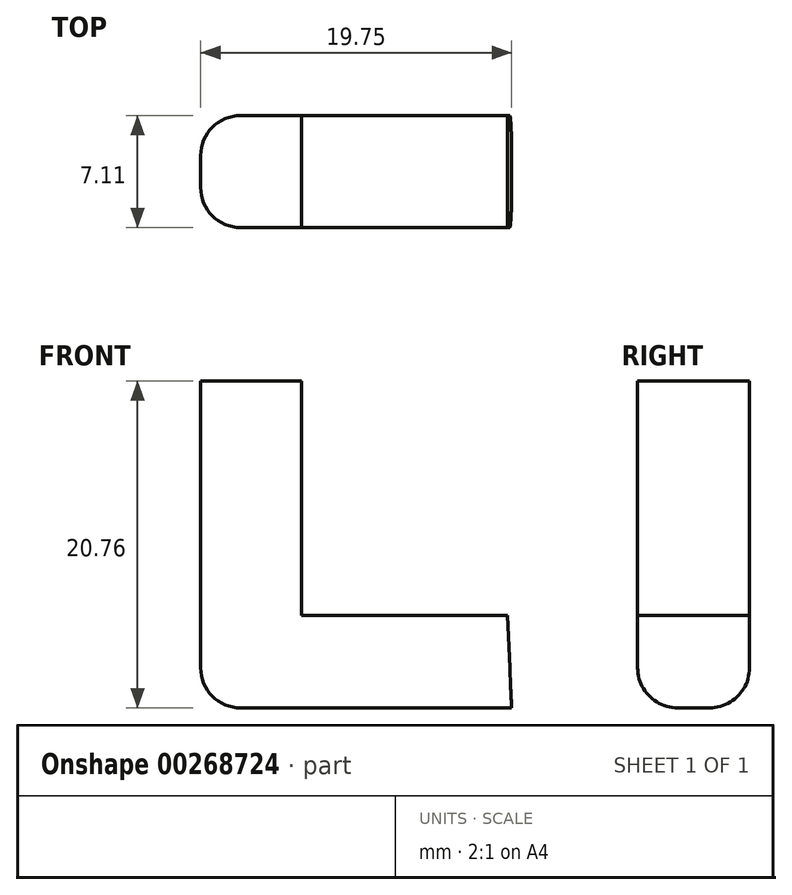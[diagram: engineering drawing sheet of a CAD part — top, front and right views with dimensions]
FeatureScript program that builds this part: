
annotation { "Feature Type Name" : "Feature", "Feature Type Description" : "" }
export const myFeature = defineFeature(function(context is Context, id is Id, definition is map)
    precondition{}
    {
        {
            var Q0;
            Q0=qCreatedBy(makeId("Front.planeOp"),FACE);
            var sketch = newSketch(context, id + "F0", { "sketchPlane" : qUnion([Q0])});
            skLineSegment(sketch, "E0", {"start": v(-9.11, -17.97) * mm, "end": v(-28.86, -17.97) * mm});
            skLineSegment(sketch, "E1", {"start": v(-28.86, -17.97) * mm, "end": v(-28.86, 2.8) * mm});
            skLineSegment(sketch, "E2", {"start": v(-28.86, 2.8) * mm, "end": v(-22.45, 2.8) * mm});
            skLineSegment(sketch, "E3", {"start": v(-22.45, 2.8) * mm, "end": v(-22.45, -12.1) * mm});
            skLineSegment(sketch, "E4", {"start": v(-22.45, -12.1) * mm, "end": v(-9.39, -12.1) * mm});
            skLineSegment(sketch, "E5", {"start": v(-9.39, -12.1) * mm, "end": v(-9.11, -17.97) * mm});
            skSolve(sketch);
        }
        {
            var Q0;
            Q0=makeQuery(id+"F0.imprint","IMPRINT",FACE,{"disambiguationData":[TD([[makeQuery(id+"F0.imprint","IMPRINT",EDGE,{"derivedFrom":sQuery(id+"F0.wireOp",EDGE,"E0")}),-1.0]])]});
            extrude(context, id + "F1", {"entities" : qUnion([Q0]), "depth" : 7.11 * mm});
        }
        {
            var Q0;
            Q0=makeQuery(id+"F1.opExtrude","CAP_EDGE",EDGE,{"disambiguationData":[OSD([sQuery(id+"F0.wireOp",EDGE,"E1")])],"isStart":false});
            fillet(context, id + "F2", {"entities" : qUnion([Q0]), "radius" : 2.54 * mm, "tangentPropagation" : true, "allowEdgeOverflow" : false});
        }
        {
            var Q0;
            Q0=makeQuery(id+"F1.opExtrude","CAP_EDGE",EDGE,{"disambiguationData":[OSD([sQuery(id+"F0.wireOp",EDGE,"E1")])],"isStart":true});
            var Q1;
            Q1=makeQuery(id+"F1.opExtrude","CAP_EDGE",EDGE,{"disambiguationData":[OSD([sQuery(id+"F0.wireOp",EDGE,"E0")])],"isStart":true});
            var Q2;
            Q2=makeQuery(id+"F1.opExtrude","CAP_EDGE",EDGE,{"disambiguationData":[OSD([sQuery(id+"F0.wireOp",EDGE,"E0")])],"isStart":false});
            fillet(context, id + "F3", {"entities" : qUnion([Q0, Q1, Q2]), "radius" : 2.54 * mm, "tangentPropagation" : true, "allowEdgeOverflow" : false});
        }
    });
